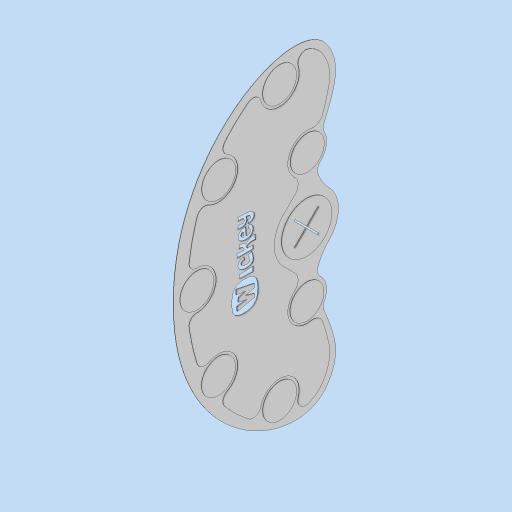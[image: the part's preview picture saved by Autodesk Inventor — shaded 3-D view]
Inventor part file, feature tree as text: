
AUTODESK INVENTOR PART (.ipt)
format: ipt  version: 2024 (Build 280153000, 153)  size: 2,113,024 bytes
history: native  units: mm
features: extrude x2, sketch x1
ambient origin geometry x8: Origin, YZ Plane, XZ Plane, XY Plane, X Axis, Y Axis, Z Axis, Center Point
bodies: Body1 (feature_tree)
feature tree (3):
  sketch  "Sketch1"  dims[d76=0.5mm d77=0.5mm d78=0.5mm d79=0.5mm d80=0.25mm d81=0.0mm d82=0.5mm d83=0.0mm d6=0.5mm d7=0.872665mm d8=0.5mm d9=0.872665mm]
  extrude  "Extrusion25"  Depth=0.5mm
  extrude  "Extrusion26"  Depth=0.5mm
